# Revit family: Drain_Deck_Parking_Zurn-Z534-Heavy-Duty
name_source: partatom
category: Plumbing Fixtures
units: mm (PartAtom-declared; Revit-internal decimal feet)

## family parameters
Always vertical = Yes
Cut with Voids When Loaded = No
Maintain Annotation Orientation = No
OmniClass Number = 23.45.55.21
OmniClass Title = Drains (Wastes)
Part Type = Normal
Room Calculation Point = No
Round Connector Dimension = Use Radius
Shared = No
Work Plane-Based = No

## types (48) — shared parameters
Assembly Code = D2030300
CW Connection = No
Default Elevation = 4 "
Description = 12-1/4 [311] DIAMETER HEAVY-DUTY PARKING DECK DRAIN WITH SUPPORT FLANGE
Grate Open Area (Sq. In) = 30
HW Connection = No
Main Material = Iron - Zurn - Cast - Painted - Blue
Manufacturer = Zurn Water, LLC
Manufacurer Brand = Zurn
Modified Date = 12/08/2025
Product Documentation Link = https://files.zurn.com
Product Installation Sheet URL = https://files.zurn.com
Product Page URL = https://www.zurn.com
Product data url = https://www.bimobject.com
Trap Primer = Yes
URL = www.zurn.com
Vent Connection = No
Waste Connection = Yes
zero-valued in all types: CWFU, HWFU, WFU

## per-type parameters (varying)
| type | A_ Pipe Size (Actual-Inner) | A_ Pipe Size (Actual-Outer) | A_ Pipe Size (Nominal) | Approx. Weight (Lbs) | Connector Radius | E_ Body Height | Frame Height | Grate Material | Top Grate diameter | Top diameter | Type Comments | ZN-Top |
| Z534-3IC | 3.068 " | 3.5 " | 3 " | 78 " | 1.5 " | 5.25 " | 2 " | Iron - Zurn - Cast - Painted - Blue | 11.25 " | 12.25 " | Z534-3 Inch Inside Caulk Outlet | No |
| Z534-4IC | 4.026 " | 4.5 " | 4 " | 78 " | 2 " | 5.25 " | 2 " | Iron - Zurn - Cast - Painted - Blue | 11.25 " | 12.25 " | Z534-4 Inch Inside Caulk Outlet | No |
| Z534-6IC | 6.065 " | 6.625 " | 6 " | 78 " | 3 " | 5.25 " | 2 " | Iron - Zurn - Cast - Painted - Blue | 11.25 " | 12.25 " | Z534-6 Inch Inside Caulk Outlet | No |
| Z534-2IP | 2.067 " | 2.375 " | 2 " | 78 " | 1 " | 3.75 " | 2 " | Iron - Zurn - Cast - Painted - Blue | 11.25 " | 12.25 " | Z534-2 Inch Threaded Outlet | No |
| Z534-3IP | 3.068 " | 3.5 " | 3 " | 78 " | 1.5 " | 3.75 " | 2 " | Iron - Zurn - Cast - Painted - Blue | 11.25 " | 12.25 " | Z534-3 Inch Threaded Outlet | No |
| Z534-4IP | 4.026 " | 4.5 " | 4 " | 78 " | 2 " | 3.75 " | 2 " | Iron - Zurn - Cast - Painted - Blue | 11.25 " | 12.25 " | Z534-4 Inch Threaded Outlet | No |
| Z534-6IP | 6.065 " | 6.625 " | 6 " | 78 " | 3 " | 3.75 " | 2 " | Iron - Zurn - Cast - Painted - Blue | 11.25 " | 12.25 " | Z534-6 Inch Threaded Outlet | No |
| Z534-8IP | 7.981 " | 8.625 " | 8 " | 80 " | 4 " | 3.75 " | 2 " | Iron - Zurn - Cast - Painted - Blue | 11.25 " | 12.25 " | Z534-8 Inch Threaded Outlet | No |
| Z534-2NH | 2.067 " | 2.375 " | 2 " | 78 " | 1 " | 5.25 " | 2 " | Iron - Zurn - Cast - Painted - Blue | 11.25 " | 12.25 " | Z534-2 Inch No-Hub Outlet | No |
| Z534-3NH | 3.068 " | 3.5 " | 3 " | 78 " | 1.5 " | 5.25 " | 2 " | Iron - Zurn - Cast - Painted - Blue | 11.25 " | 12.25 " | Z534-3 Inch No-Hub Outlet | No |
| Z534-4NH | 4.026 " | 4.5 " | 4 " | 78 " | 2 " | 5.25 " | 2 " | Iron - Zurn - Cast - Painted - Blue | 11.25 " | 12.25 " | Z534-4 Inch No-Hub Outlet | No |
| Z534-6NH | 6.065 " | 6.625 " | 6 " | 78 " | 3 " | 5.25 " | 2 " | Iron - Zurn - Cast - Painted - Blue | 11.25 " | 12.25 " | Z534-6 Inch No-Hub Outlet | No |
| Z534-8NH | 7.981 " | 8.625 " | 8 " | 78 " | 4 " | 5.25 " | 2 " | Iron - Zurn - Cast - Painted - Blue | 11.25 " | 12.25 " | Z534-8 Inch No-Hub Outlet | No |
| Z534-2NL | 2.067 " | 2.375 " | 2 " | 78 " | 1 " | 4.625 " | 2 " | Iron - Zurn - Cast - Painted - Blue | 11.25 " | 12.25 " | Z534-2 Inch Neo-Loc Outlet | No |
| Z534-3NL | 3.068 " | 3.5 " | 3 " | 78 " | 1.5 " | 4.625 " | 2 " | Iron - Zurn - Cast - Painted - Blue | 11.25 " | 12.25 " | Z534-3 Inch Neo-Loc Outlet | No |
| Z534-4NL | 4.026 " | 4.5 " | 4 " | 78 " | 2 " | 4.625 " | 2 " | Iron - Zurn - Cast - Painted - Blue | 11.25 " | 12.25 " | Z534-4 Inch Neo-Loc Outlet | No |
| ZN534-3IC | 3.068 " | 3.5 " | 3 " | 78 " | 1.5 " | 5.25 " | 2.188 " | Bronze - Zurn - Polished Nickel | 12 " | 13 " | ZN534-3 Inch Inside Caulk Outlet with Polished Nickel Bronze Top | Yes |
| ZN534-4IC | 4.026 " | 4.5 " | 4 " | 78 " | 2 " | 5.25 " | 2.188 " | Bronze - Zurn - Polished Nickel | 12 " | 13 " | ZN534-4 Inch Inside Caulk Outlet with Polished Nickel Bronze Top | Yes |
| ZN534-6IC | 6.065 " | 6.625 " | 6 " | 78 " | 3 " | 5.25 " | 2.188 " | Bronze - Zurn - Polished Nickel | 12 " | 13 " | ZN534-6 Inch Inside Caulk Outlet with Polished Nickel Bronze Top | Yes |
| ZN534-2IP | 2.067 " | 2.375 " | 2 " | 78 " | 1 " | 3.75 " | 2.188 " | Bronze - Zurn - Polished Nickel | 12 " | 13 " | ZN534-2 Inch Threaded Outlet with Polished Nickel Bronze Top | Yes |
| ZN534-3IP | 3.068 " | 3.5 " | 3 " | 78 " | 1.5 " | 3.75 " | 2.188 " | Bronze - Zurn - Polished Nickel | 12 " | 13 " | ZN534-3 Inch Threaded Outlet with Polished Nickel Bronze Top | Yes |
| ZN534-4IP | 4.026 " | 4.5 " | 4 " | 78 " | 2 " | 3.75 " | 2.188 " | Bronze - Zurn - Polished Nickel | 12 " | 13 " | ZN534-4 Inch Threaded Outlet with Polished Nickel Bronze Top | Yes |
| ZN534-6IP | 6.065 " | 6.625 " | 6 " | 78 " | 3 " | 3.75 " | 2.188 " | Bronze - Zurn - Polished Nickel | 12 " | 13 " | ZN534-6 Inch Threaded Outlet with Polished Nickel Bronze Top | Yes |
| ZN534-8IP | 7.981 " | 8.625 " | 8 " | 80 " | 4 " | 3.75 " | 2.188 " | Bronze - Zurn - Polished Nickel | 12 " | 13 " | ZN534-8 Inch Threaded Outlet with Polished Nickel Bronze Top | Yes |
| ZN534-2NH | 2.067 " | 2.375 " | 2 " | 78 " | 1 " | 5.25 " | 2.188 " | Bronze - Zurn - Polished Nickel | 12 " | 13 " | ZN534-2 Inch No-Hub Outlet with Polished Nickel Bronze Top | Yes |
| ZN534-3NH | 3.068 " | 3.5 " | 3 " | 78 " | 1.5 " | 5.25 " | 2.188 " | Bronze - Zurn - Polished Nickel | 12 " | 13 " | ZN534-3 Inch No-Hub Outlet with Polished Nickel Bronze Top | Yes |
| ZN534-4NH | 4.026 " | 4.5 " | 4 " | 78 " | 2 " | 5.25 " | 2.188 " | Bronze - Zurn - Polished Nickel | 12 " | 13 " | ZN534-4 Inch No-Hub Outlet with Polished Nickel Bronze Top | Yes |
| ZN534-6NH | 6.065 " | 6.625 " | 6 " | 78 " | 3 " | 5.25 " | 2.188 " | Bronze - Zurn - Polished Nickel | 12 " | 13 " | ZN534-6 Inch No-Hub Outlet with Polished Nickel Bronze Top | Yes |
| ZN534-8NH | 7.981 " | 8.625 " | 8 " | 78 " | 4 " | 5.25 " | 2.188 " | Bronze - Zurn - Polished Nickel | 12 " | 13 " | ZN534-8 Inch No-Hub Outlet with Polished Nickel Bronze Top | Yes |
| ZN534-2NL | 2.067 " | 2.375 " | 2 " | 78 " | 1 " | 4.625 " | 2.188 " | Bronze - Zurn - Polished Nickel | 12 " | 13 " | ZN534-2 Inch Neo-Loc Outlet with Polished Nickel Bronze Top | Yes |
| ZN534-3NL | 3.068 " | 3.5 " | 3 " | 78 " | 1.5 " | 4.625 " | 2.188 " | Bronze - Zurn - Polished Nickel | 12 " | 13 " | ZN534-3 Inch Neo-Loc Outlet with Polished Nickel Bronze Top | Yes |
| ZN534-4NL | 4.026 " | 4.5 " | 4 " | 78 " | 2 " | 4.625 " | 2.188 " | Bronze - Zurn - Polished Nickel | 12 " | 13 " | ZN534-4 Inch Neo-Loc Outlet with Polished Nickel Bronze Top | Yes |
| ZB534-3IC | 3.068 " | 3.5 " | 3 " | 78 " | 1.5 " | 5.25 " | 2.188 " | Bronze - Zurn - Polished | 12 " | 13 " | ZB534-3 Inch Inside Caulk Outlet with Polished Nickel Bronze Top | Yes |
| ZB534-4IC | 4.026 " | 4.5 " | 4 " | 78 " | 2 " | 5.25 " | 2.188 " | Bronze - Zurn - Polished | 12 " | 13 " | ZB534-4 Inch Inside Caulk Outlet with Polished Nickel Bronze Top | Yes |
| ZB534-6IC | 6.065 " | 6.625 " | 6 " | 78 " | 3 " | 5.25 " | 2.188 " | Bronze - Zurn - Polished | 12 " | 13 " | ZB534-6 Inch Inside Caulk Outlet with Polished Nickel Bronze Top | Yes |
| ZB534-2IP | 2.067 " | 2.375 " | 2 " | 78 " | 1 " | 3.75 " | 2.188 " | Bronze - Zurn - Polished | 12 " | 13 " | ZB534-2 Inch Threaded Outlet with Polished Nickel Bronze Top | Yes |
| ZB534-3IP | 3.068 " | 3.5 " | 3 " | 78 " | 1.5 " | 3.75 " | 2.188 " | Bronze - Zurn - Polished | 12 " | 13 " | ZB534-3 Inch Threaded Outlet with Polished Nickel Bronze Top | Yes |
| ZB534-4IP | 4.026 " | 4.5 " | 4 " | 78 " | 2 " | 3.75 " | 2.188 " | Bronze - Zurn - Polished | 12 " | 13 " | ZB534-4 Inch Threaded Outlet with Polished Nickel Bronze Top | Yes |
| ZB534-6IP | 6.065 " | 6.625 " | 6 " | 78 " | 3 " | 3.75 " | 2.188 " | Bronze - Zurn - Polished | 12 " | 13 " | ZB534-6 Inch Threaded Outlet with Polished Nickel Bronze Top | Yes |
| ZB534-8IP | 7.981 " | 8.625 " | 8 " | 80 " | 4 " | 3.75 " | 2.188 " | Bronze - Zurn - Polished | 12 " | 13 " | ZB534-8 Inch Threaded Outlet with Polished Nickel Bronze Top | Yes |
| ZB534-2NH | 2.067 " | 2.375 " | 2 " | 78 " | 1 " | 5.25 " | 2.188 " | Bronze - Zurn - Polished | 12 " | 13 " | ZB534-2 Inch No-Hub Outlet with Polished Nickel Bronze Top | Yes |
| ZB534-3NH | 3.068 " | 3.5 " | 3 " | 78 " | 1.5 " | 5.25 " | 2.188 " | Bronze - Zurn - Polished | 12 " | 13 " | ZB534-3 Inch No-Hub Outlet with Polished Nickel Bronze Top | Yes |
| ZB534-4NH | 4.026 " | 4.5 " | 4 " | 78 " | 2 " | 5.25 " | 2.188 " | Bronze - Zurn - Polished | 12 " | 13 " | ZB534-4 Inch No-Hub Outlet with Polished Nickel Bronze Top | Yes |
| ZB534-6NH | 6.065 " | 6.625 " | 6 " | 78 " | 3 " | 5.25 " | 2.188 " | Bronze - Zurn - Polished | 12 " | 13 " | ZB534-6 Inch No-Hub Outlet with Polished Nickel Bronze Top | Yes |
| ZB534-8NH | 7.981 " | 8.625 " | 8 " | 78 " | 4 " | 5.25 " | 2.188 " | Bronze - Zurn - Polished | 12 " | 13 " | ZB534-8 Inch No-Hub Outlet with Polished Nickel Bronze Top | Yes |
| ZB534-2NL | 2.067 " | 2.375 " | 2 " | 78 " | 1 " | 4.625 " | 2.188 " | Bronze - Zurn - Polished | 12 " | 13 " | ZB534-2 Inch Neo-Loc Outlet with Polished Nickel Bronze Top | Yes |
| ZB534-3NL | 3.068 " | 3.5 " | 3 " | 78 " | 1.5 " | 4.625 " | 2.188 " | Bronze - Zurn - Polished | 12 " | 13 " | ZB534-3 Inch Neo-Loc Outlet with Polished Nickel Bronze Top | Yes |
| ZB534-4NL | 4.026 " | 4.5 " | 4 " | 78 " | 2 " | 4.625 " | 2.188 " | Bronze - Zurn - Polished | 12 " | 13 " | ZB534-4 Inch Neo-Loc Outlet with Polished Nickel Bronze Top | Yes |

note: column(s) folded — value = type name in every type: Model

## geometry (parser evidence)
native form markers: Blend x8, Sweep x4
no freeform markers — native parametric forms only
